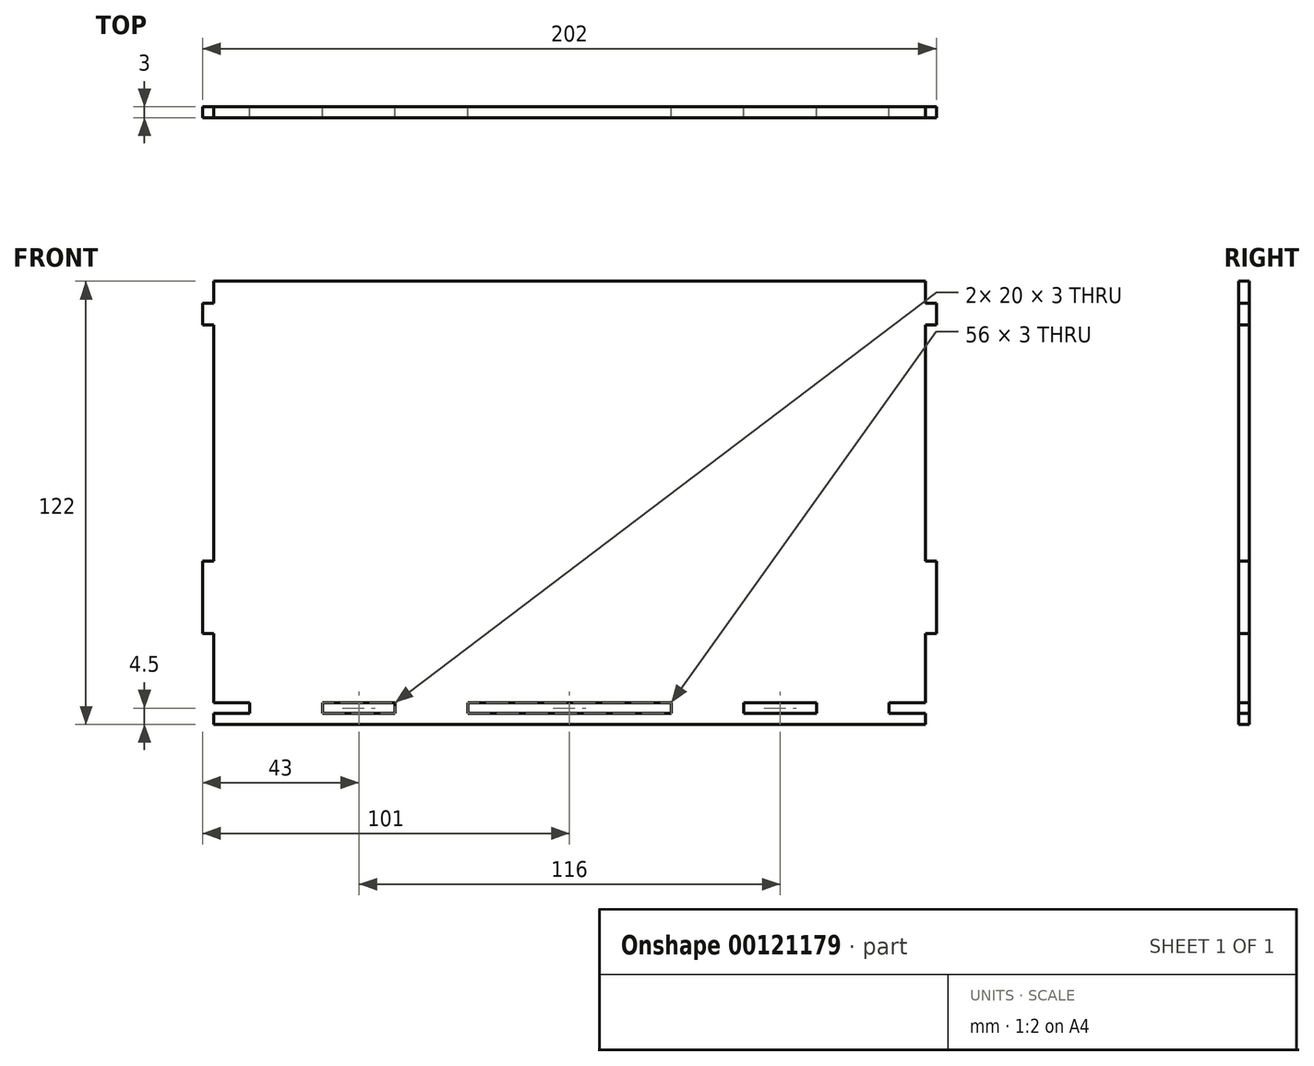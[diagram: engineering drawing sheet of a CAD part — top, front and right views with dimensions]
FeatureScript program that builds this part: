
annotation { "Feature Type Name" : "Feature", "Feature Type Description" : "" }
export const myFeature = defineFeature(function(context is Context, id is Id, definition is map)
    precondition{}
    {
        {
            var Q0;
            Q0=qCreatedBy(makeId("Front.planeOp"),FACE);
            var sketch = newSketch(context, id + "F0", { "sketchPlane" : qUnion([Q0])});
            skPoint(sketch, "E0.middle", {"position": v(0, 0) * mm});
            skLineSegment(sketch, "E1", {"start": v(-88, -56.5) * mm, "end": v(-88, -59.5) * mm});
            skLineSegment(sketch, "E2", {"start": v(-88, -56.5) * mm, "end": v(-98, -56.5) * mm});
            skLineSegment(sketch, "E3", {"start": v(-98, -59.5) * mm, "end": v(-98, -62.5) * mm});
            skLineSegment(sketch, "E4", {"start": v(-98, -59.5) * mm, "end": v(-88, -59.5) * mm});
            skLineSegment(sketch, "E5", {"start": v(-98, -59.5) * mm, "end": v(-98, -59.5) * mm});
            skLineSegment(sketch, "E6", {"start": v(-98, -62.5) * mm, "end": v(0, -62.5) * mm});
            skLineSegment(sketch, "E7.bottom", {"start": v(-68, -56.5) * mm, "end": v(-48, -56.5) * mm});
            skLineSegment(sketch, "E7.top", {"start": v(-68, -59.5) * mm, "end": v(-48, -59.5) * mm});
            skLineSegment(sketch, "E7.left", {"start": v(-68, -56.5) * mm, "end": v(-68, -59.5) * mm});
            skLineSegment(sketch, "E7.right", {"start": v(-48, -56.5) * mm, "end": v(-48, -59.5) * mm});
            skLineSegment(sketch, "E8", {"start": v(98, -62.5) * mm, "end": v(98, -59.5) * mm});
            skLineSegment(sketch, "E9", {"start": v(98, -59.5) * mm, "end": v(88, -59.5) * mm});
            skLineSegment(sketch, "E10", {"start": v(88, -59.5) * mm, "end": v(88, -56.5) * mm});
            skLineSegment(sketch, "E11", {"start": v(88, -56.5) * mm, "end": v(98, -56.5) * mm});
            skLineSegment(sketch, "E12.bottom", {"start": v(48, -56.5) * mm, "end": v(68, -56.5) * mm});
            skLineSegment(sketch, "E12.top", {"start": v(48, -59.5) * mm, "end": v(68, -59.5) * mm});
            skLineSegment(sketch, "E12.left", {"start": v(48, -56.5) * mm, "end": v(48, -59.5) * mm});
            skLineSegment(sketch, "E12.right", {"start": v(68, -56.5) * mm, "end": v(68, -59.5) * mm});
            skLineSegment(sketch, "E13.bottom", {"start": v(-28, -56.5) * mm, "end": v(28, -56.5) * mm});
            skLineSegment(sketch, "E13.top", {"start": v(-28, -59.5) * mm, "end": v(28, -59.5) * mm});
            skLineSegment(sketch, "E13.left", {"start": v(-28, -56.5) * mm, "end": v(-28, -59.5) * mm});
            skLineSegment(sketch, "E13.right", {"start": v(28, -56.5) * mm, "end": v(28, -59.5) * mm});
            skLineSegment(sketch, "E14", {"start": v(101, 53.5) * mm, "end": v(101, 47.5) * mm});
            skLineSegment(sketch, "E15", {"start": v(-98, -37.5) * mm, "end": v(-101, -37.5) * mm});
            skLineSegment(sketch, "E16", {"start": v(-98, -37.5) * mm, "end": v(-98, -56.5) * mm});
            skLineSegment(sketch, "E17", {"start": v(-101, -17.5) * mm, "end": v(-98, -17.5) * mm});
            skLineSegment(sketch, "E18", {"start": v(-101, 47.5) * mm, "end": v(-98, 47.5) * mm});
            skLineSegment(sketch, "E19", {"start": v(-101, -17.5) * mm, "end": v(-101, -37.5) * mm});
            skLineSegment(sketch, "E20", {"start": v(-98, 47.5) * mm, "end": v(-98, -17.5) * mm});
            skLineSegment(sketch, "E21.0", {"start": v(-98, 59.5) * mm, "end": v(0, 59.5) * mm});
            skLineSegment(sketch, "E22", {"start": v(-98, 47.5) * mm, "end": v(-101, 47.5) * mm});
            skLineSegment(sketch, "E23", {"start": v(-101, 47.5) * mm, "end": v(-101, 53.5) * mm});
            skLineSegment(sketch, "E24", {"start": v(-101, 53.5) * mm, "end": v(-98, 53.5) * mm});
            skLineSegment(sketch, "E25", {"start": v(-98, 53.5) * mm, "end": v(-98, 59.5) * mm});
            skLineSegment(sketch, "E26", {"start": v(98, 59.5) * mm, "end": v(98, 53.5) * mm});
            skLineSegment(sketch, "E27", {"start": v(101, 47.5) * mm, "end": v(98, 47.5) * mm});
            skLineSegment(sketch, "E28", {"start": v(98, -56.5) * mm, "end": v(98, -37.5) * mm});
            skLineSegment(sketch, "E29", {"start": v(98, -37.5) * mm, "end": v(101, -37.5) * mm});
            skLineSegment(sketch, "E30", {"start": v(101, -17.5) * mm, "end": v(98, -17.5) * mm});
            skLineSegment(sketch, "E31", {"start": v(98, -17.5) * mm, "end": v(98, 47.5) * mm});
            skLineSegment(sketch, "E32", {"start": v(101, -17.5) * mm, "end": v(101, -37.5) * mm});
            skLineSegment(sketch, "E33", {"start": v(0, -62.5) * mm, "end": v(98, -62.5) * mm});
            skLineSegment(sketch, "E34", {"start": v(0, 59.5) * mm, "end": v(98, 59.5) * mm});
            skLineSegment(sketch, "E35", {"start": v(101, 53.5) * mm, "end": v(98, 53.5) * mm});
            skSolve(sketch);
        }
        {
            var Q0;
            Q0 = qSketchRegion(id + "F0", true);
            extrude(context, id + "F1", {"entities" : qUnion([Q0]), "endBound" : BoundingType.SYMMETRIC, "depth" : 3 * mm});
        }
    });
